# Revit family: Haworth_Mex-Hi_Sofa_ExtraWide
name_source: partatom
category: Furniture
revit_build: Autodesk Revit 2018 (Build: 20170223_1515(x64)
units: mm (PartAtom-declared; Revit-internal decimal feet)

## family parameters
Always vertical = Yes
Cut with Voids When Loaded = No
OmniClass Number = 23.40.70.14.64.21
OmniClass Title = Systems Furniture
Room Calculation Point = No
Shared = No
Work Plane-Based = No

## types (3) — shared parameters
Actual Depth = 35.5 "
Actual Height = 28.3 "
Actual Width = 122 "
Assembly Code = E2020200
Manufacturer = Haworth
Model = HCCSMHL
Revision Number = 1
Size = Verify Final Dim. w/ Haworth
Sustainability Info = https://www.haworth.com
Trim Finish = Haworth _ Polymer _ Black
URL = https://www.haworth.com
URL - Product = https://www.haworth.com
Warranty = http://www.haworth.com

## per-type parameters (varying)
| type | Description | Left Arms | Right Arms | With Arms | Without Arms |
| Three Seat Sofa - Two Arms | Haworth - Cassina - Mex-Hi - Sofa - Two Arms - Extra Wide Three Seat | Yes | Yes | Yes | No |
| Three Seat Sofa - One Arm | Haworth - Cassina - Mex-Hi - Sofa - One Arm - Extra Wide Three Seat | Yes | No | No | Yes |
| Three Seat Sofa - Without Arm | Haworth - Cassina - Mex-Hi - Sofa - Without Arm - Extra Wide Three Seat | No | No | No | Yes |

## geometry (parser evidence)
native form markers: Sweep x16
no freeform markers — native parametric forms only
